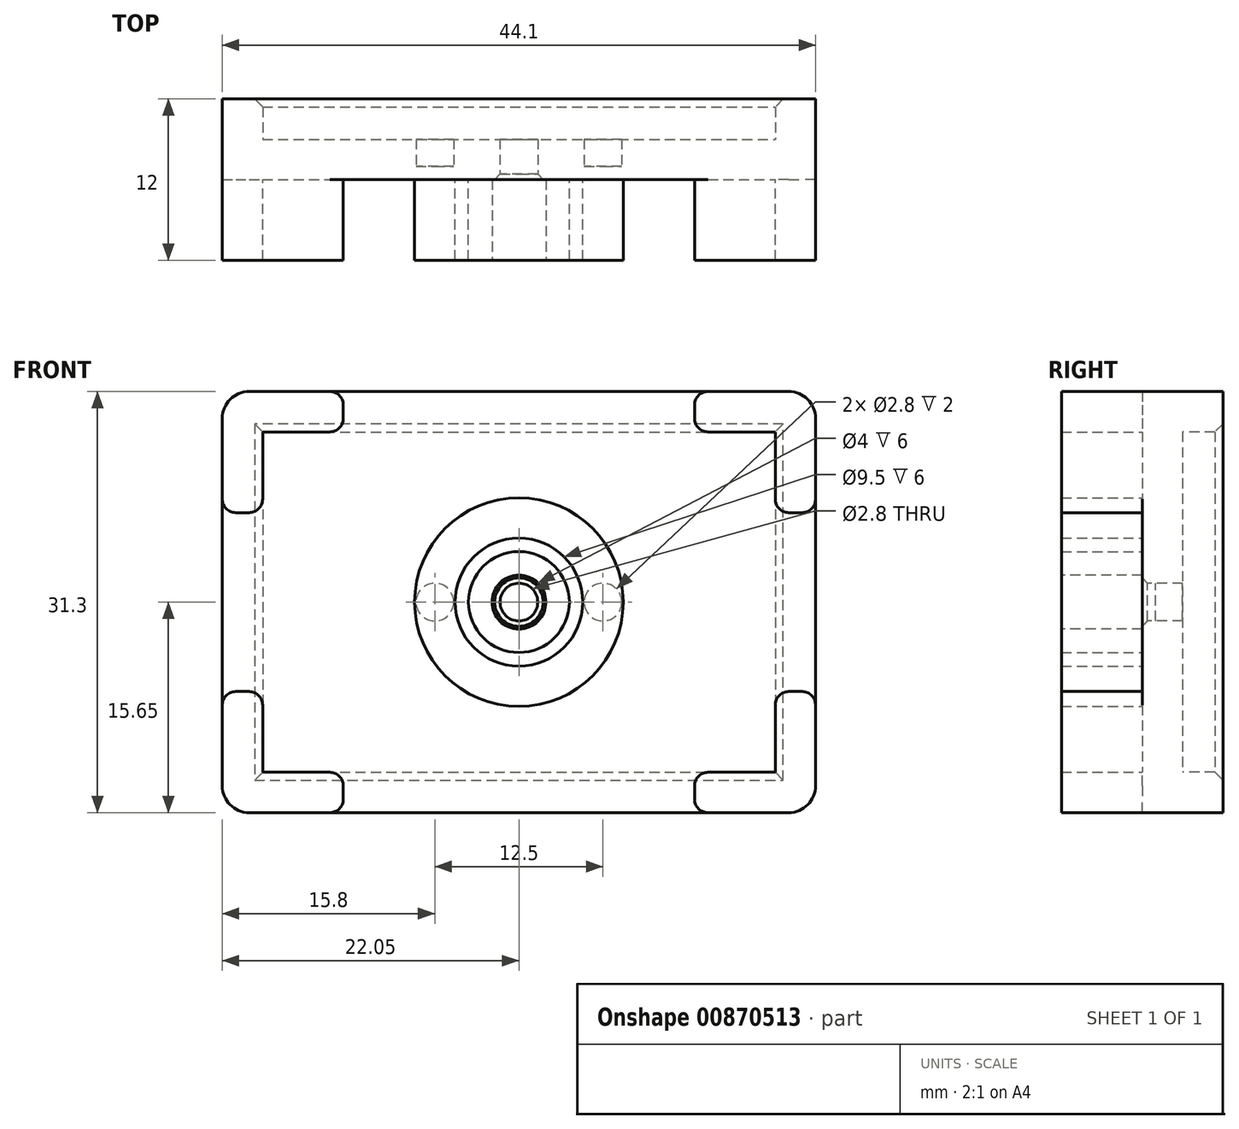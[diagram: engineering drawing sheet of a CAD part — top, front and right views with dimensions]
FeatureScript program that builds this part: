
annotation { "Feature Type Name" : "Feature", "Feature Type Description" : "" }
export const myFeature = defineFeature(function(context is Context, id is Id, definition is map)
    precondition{}
    {
        {
            var Q0;
            Q0=qCreatedBy(makeId("Front.planeOp"),FACE);
            var sketch = newSketch(context, id + "F0", { "sketchPlane" : qUnion([Q0])});
            skLineSegment(sketch, "E0.bottom", {"start": v(-19.05, 12.65) * mm, "end": v(19.05, 12.65) * mm});
            skLineSegment(sketch, "E0.top", {"start": v(-19.05, -12.65) * mm, "end": v(19.05, -12.65) * mm});
            skLineSegment(sketch, "E0.left", {"start": v(-19.05, 12.65) * mm, "end": v(-19.05, -12.65) * mm});
            skLineSegment(sketch, "E0.right", {"start": v(19.05, 12.65) * mm, "end": v(19.05, -12.65) * mm});
            skPoint(sketch, "E0.middle", {"position": v(0, 0) * mm});
            skLineSegment(sketch, "E1.bottom", {"start": v(-22.05, 15.65) * mm, "end": v(22.05, 15.65) * mm});
            skLineSegment(sketch, "E1.top", {"start": v(-22.05, -15.65) * mm, "end": v(22.05, -15.65) * mm});
            skLineSegment(sketch, "E1.left", {"start": v(-22.05, 15.65) * mm, "end": v(-22.05, -15.65) * mm});
            skLineSegment(sketch, "E1.right", {"start": v(22.05, 15.65) * mm, "end": v(22.05, -15.65) * mm});
            skCircle(sketch, "E2", {"center": v(-6.25, 0) * mm, "radius": 1.4 * mm});
            skCircle(sketch, "E3", {"center": v(6.25, 0) * mm, "radius": 1.4 * mm});
            skCircle(sketch, "E4", {"center": v(0, 0) * mm, "radius": 2 * mm});
            skCircle(sketch, "E5", {"center": v(0, 0) * mm, "radius": 4.75 * mm});
            skCircle(sketch, "E6", {"center": v(0, 0) * mm, "radius": 3.75 * mm});
            skCircle(sketch, "E7", {"center": v(0, 0) * mm, "radius": 9.5 * mm});
            skCircle(sketch, "E8", {"center": v(0, 0) * mm, "radius": 7.75 * mm});
            skCircle(sketch, "E9", {"center": v(0, 0) * mm, "radius": 1.4 * mm});
            skLineSegment(sketch, "E10.bottom", {"start": v(-13.05, -12.65) * mm, "end": v(13.05, -12.65) * mm});
            skLineSegment(sketch, "E10.top", {"start": v(-13.05, -15.65) * mm, "end": v(13.05, -15.65) * mm});
            skLineSegment(sketch, "E10.left", {"start": v(-13.05, -12.65) * mm, "end": v(-13.05, -15.65) * mm});
            skLineSegment(sketch, "E10.right", {"start": v(13.05, -12.65) * mm, "end": v(13.05, -15.65) * mm});
            skLineSegment(sketch, "E11.bottom", {"start": v(-13.05, 15.65) * mm, "end": v(13.05, 15.65) * mm});
            skLineSegment(sketch, "E11.top", {"start": v(-13.05, 12.65) * mm, "end": v(13.05, 12.65) * mm});
            skLineSegment(sketch, "E11.left", {"start": v(-13.05, 15.65) * mm, "end": v(-13.05, 12.65) * mm});
            skLineSegment(sketch, "E11.right", {"start": v(13.05, 15.65) * mm, "end": v(13.05, 12.65) * mm});
            skLineSegment(sketch, "E12.bottom", {"start": v(-22.05, -6.65) * mm, "end": v(-19.05, -6.65) * mm});
            skLineSegment(sketch, "E12.top", {"start": v(-22.05, 6.65) * mm, "end": v(-19.05, 6.65) * mm});
            skLineSegment(sketch, "E12.left", {"start": v(-22.05, -6.65) * mm, "end": v(-22.05, 6.65) * mm});
            skLineSegment(sketch, "E12.right", {"start": v(-19.05, -6.65) * mm, "end": v(-19.05, 6.65) * mm});
            skLineSegment(sketch, "E13.bottom", {"start": v(19.05, 6.65) * mm, "end": v(22.05, 6.65) * mm});
            skLineSegment(sketch, "E13.top", {"start": v(19.05, -6.65) * mm, "end": v(22.05, -6.65) * mm});
            skLineSegment(sketch, "E13.left", {"start": v(19.05, 6.65) * mm, "end": v(19.05, -6.65) * mm});
            skLineSegment(sketch, "E13.right", {"start": v(22.05, 6.65) * mm, "end": v(22.05, -6.65) * mm});
            skSolve(sketch);
        }
        {
            var Q0;
            Q0=makeQuery(id+"F0.imprint","IMPRINT",FACE,{"disambiguationData":[TD([[makeQuery(id+"F0.imprint","IMPRINT",EDGE,{"derivedFrom":sQuery(id+"F0.wireOp",EDGE,"E7")}),-1.0]])]});
            var Q1;
            Q1=makeQuery(id+"F0.imprint","IMPRINT",FACE,{"disambiguationData":[TD([[makeQuery(id+"F0.imprint","IMPRINT",EDGE,{"derivedFrom":sQuery(id+"F0.wireOp",EDGE,"E4")}),-1.0]])]});
            var Q2;
            Q2=makeQuery(id+"F0.imprint","IMPRINT",FACE,{"disambiguationData":[TD([[makeQuery(id+"F0.imprint","IMPRINT",EDGE,{"derivedFrom":sQuery(id+"F0.wireOp",EDGE,"E5")}),1.0]])]});
            var Q3;
            Q3=makeQuery(id+"F0.imprint","IMPRINT",FACE,{"disambiguationData":[TD([[makeQuery(id+"F0.imprint","IMPRINT",EDGE,{"derivedFrom":sQuery(id+"F0.wireOp",EDGE,"E2")}),-1.0]])]});
            var Q4;
            Q4=makeQuery(id+"F0.imprint","IMPRINT",FACE,{"disambiguationData":[TD([[makeQuery(id+"F0.imprint","IMPRINT",EDGE,{"derivedFrom":sQuery(id+"F0.wireOp",EDGE,"E7")}),1.0]])]});
            extrude(context, id + "F1", {"entities" : qUnion([Q0, Q1, Q2, Q3, Q4]), "oppositeDirection" : true, "depth" : 3 * mm, "offsetDistance" : 25 * mm});
        }
        {
            var Q0;
            {var subQ7=sQuery(id+"F0.wireOp",EDGE,"E11.right");var subQ13=sQuery(id+"F0.wireOp",EDGE,"E11.left");Q0=qUnion([makeQuery(id+"F0.imprint","IMPRINT",FACE,{"disambiguationData":[TD([[makeQuery(id+"F0.imprint","IMPRINT",EDGE,{"derivedFrom":subQ13}),-1.0]])]}),makeQuery(id+"F0.imprint","IMPRINT",FACE,{"disambiguationData":[TD([[makeQuery(id+"F0.imprint","IMPRINT",EDGE,{"derivedFrom":subQ7}),1.0]])]})]);}
            var Q1;
            {var subQ0=sQuery(id+"F0.wireOp",EDGE,"E10.left");Q1=makeQuery(id+"F0.imprint","IMPRINT",FACE,{"disambiguationData":[TD([[makeQuery(id+"F0.imprint","IMPRINT",EDGE,{"derivedFrom":subQ0}),1.0]])]});}
            var Q2;
            {var subQ0=sQuery(id+"F0.wireOp",EDGE,"E11.left");Q2=makeQuery(id+"F0.imprint","IMPRINT",FACE,{"disambiguationData":[TD([[makeQuery(id+"F0.imprint","IMPRINT",EDGE,{"derivedFrom":subQ0}),1.0]])]});}
            var Q3;
            {var subQ2=sQuery(id+"F0.wireOp",EDGE,"E12.bottom");Q3=makeQuery(id+"F0.imprint","IMPRINT",FACE,{"disambiguationData":[TD([[makeQuery(id+"F0.imprint","IMPRINT",EDGE,{"derivedFrom":subQ2}),1.0]])]});}
            var Q4;
            {var subQ4=sQuery(id+"F0.wireOp",EDGE,"E10.left");Q4=makeQuery(id+"F0.imprint","IMPRINT",FACE,{"disambiguationData":[TD([[makeQuery(id+"F0.imprint","IMPRINT",EDGE,{"derivedFrom":subQ4}),-1.0]])]});}
            var Q5;
            {var subQ4=sQuery(id+"F0.wireOp",EDGE,"E10.right");Q5=makeQuery(id+"F0.imprint","IMPRINT",FACE,{"disambiguationData":[TD([[makeQuery(id+"F0.imprint","IMPRINT",EDGE,{"derivedFrom":subQ4}),1.0]])]});}
            var Q6;
            {var subQ0=sQuery(id+"F0.wireOp",EDGE,"E13.bottom");Q6=makeQuery(id+"F0.imprint","IMPRINT",FACE,{"disambiguationData":[TD([[makeQuery(id+"F0.imprint","IMPRINT",EDGE,{"derivedFrom":subQ0}),-1.0]])]});}
            extrude(context, id + "F2", {"entities" : qUnion([Q0, Q1, Q2, Q3, Q4, Q5, Q6]), "operationType" : NewBodyOperationType.ADD, "oppositeDirection" : true, "depth" : 6 * mm, "offsetDistance" : 25 * mm});
        }
        {
            var Q0;
            Q0=makeQuery(id+"F0.imprint","IMPRINT",FACE,{"disambiguationData":[TD([[makeQuery(id+"F0.imprint","IMPRINT",EDGE,{"derivedFrom":sQuery(id+"F0.wireOp",EDGE,"E2")}),1.0]])]});
            var Q1;
            Q1=makeQuery(id+"F0.imprint","IMPRINT",FACE,{"disambiguationData":[TD([[makeQuery(id+"F0.imprint","IMPRINT",EDGE,{"derivedFrom":sQuery(id+"F0.wireOp",EDGE,"E3")}),1.0]])]});
            extrude(context, id + "F3", {"entities" : qUnion([Q0, Q1]), "operationType" : NewBodyOperationType.ADD, "oppositeDirection" : true, "depth" : 1 * mm, "offsetDistance" : 25 * mm});
        }
        {
            var Q0;
            Q0=makeQuery(id+"F0.imprint","IMPRINT",FACE,{"disambiguationData":[TD([[makeQuery(id+"F0.imprint","IMPRINT",EDGE,{"derivedFrom":sQuery(id+"F0.wireOp",EDGE,"E4")}),-1.0]])]});
            extrude(context, id + "F4", {"entities" : qUnion([Q0]), "operationType" : NewBodyOperationType.ADD, "depth" : 6 * mm, "offsetDistance" : 25 * mm});
        }
        {
            var Q0;
            {var subQ7=sQuery(id+"F0.wireOp",EDGE,"E11.right");var subQ13=sQuery(id+"F0.wireOp",EDGE,"E11.left");Q0=qUnion([makeQuery(id+"F0.imprint","IMPRINT",FACE,{"disambiguationData":[TD([[makeQuery(id+"F0.imprint","IMPRINT",EDGE,{"derivedFrom":subQ13}),-1.0]])]}),makeQuery(id+"F0.imprint","IMPRINT",FACE,{"disambiguationData":[TD([[makeQuery(id+"F0.imprint","IMPRINT",EDGE,{"derivedFrom":subQ7}),1.0]])]})]);}
            var Q1;
            {var subQ4=sQuery(id+"F0.wireOp",EDGE,"E10.left");Q1=makeQuery(id+"F0.imprint","IMPRINT",FACE,{"disambiguationData":[TD([[makeQuery(id+"F0.imprint","IMPRINT",EDGE,{"derivedFrom":subQ4}),-1.0]])]});}
            var Q2;
            {var subQ4=sQuery(id+"F0.wireOp",EDGE,"E10.right");Q2=makeQuery(id+"F0.imprint","IMPRINT",FACE,{"disambiguationData":[TD([[makeQuery(id+"F0.imprint","IMPRINT",EDGE,{"derivedFrom":subQ4}),1.0]])]});}
            extrude(context, id + "F5", {"entities" : qUnion([Q0, Q1, Q2]), "operationType" : NewBodyOperationType.ADD, "depth" : 6 * mm, "offsetDistance" : 25 * mm});
        }
        {
            var Q0;
            Q0=makeQuery(id+"F0.imprint","IMPRINT",FACE,{"disambiguationData":[TD([[makeQuery(id+"F0.imprint","IMPRINT",EDGE,{"derivedFrom":sQuery(id+"F0.wireOp",EDGE,"E2")}),-1.0]])]});
            var Q1;
            Q1=makeQuery(id+"F0.imprint","IMPRINT",FACE,{"disambiguationData":[TD([[makeQuery(id+"F0.imprint","IMPRINT",EDGE,{"derivedFrom":sQuery(id+"F0.wireOp",EDGE,"E2")}),1.0]])]});
            var Q2;
            Q2=makeQuery(id+"F0.imprint","IMPRINT",FACE,{"disambiguationData":[TD([[makeQuery(id+"F0.imprint","IMPRINT",EDGE,{"derivedFrom":sQuery(id+"F0.wireOp",EDGE,"E3")}),1.0]])]});
            extrude(context, id + "F6", {"entities" : qUnion([Q0, Q1, Q2]), "operationType" : NewBodyOperationType.ADD, "depth" : 6 * mm, "offsetDistance" : 25 * mm});
        }
        {
            var Q0;
            Q0=makeQuery(id+"F2.opExtrude","CAP_EDGE",EDGE,{"disambiguationData":[OSD([sQuery(id+"F0.wireOp",EDGE,"E0.bottom")])],"isStart":false});
            var Q1;
            Q1=makeQuery(id+"F2.opExtrude","CAP_EDGE",EDGE,{"disambiguationData":[OSD([sQuery(id+"F0.wireOp",EDGE,"E0.left")])],"isStart":false});
            var Q2;
            Q2=makeQuery(id+"F2.opExtrude","CAP_EDGE",EDGE,{"disambiguationData":[OSD([sQuery(id+"F0.wireOp",EDGE,"E0.right")])],"isStart":false});
            var Q3;
            Q3=makeQuery(id+"F2.opExtrude","CAP_EDGE",EDGE,{"disambiguationData":[OSD([sQuery(id+"F0.wireOp",EDGE,"E0.top")])],"isStart":false});
            chamfer(context, id + "F7", {"entities" : qUnion([Q0, Q1, Q2, Q3]), "width" : 0.6 * mm, "tangentPropagation" : true});
        }
        {
            var Q0;
            Q0=makeQuery(id+"F0.imprint","IMPRINT",FACE,{"disambiguationData":[TD([[makeQuery(id+"F0.imprint","IMPRINT",EDGE,{"derivedFrom":sQuery(id+"F0.wireOp",EDGE,"E4")}),1.0]])]});
            extrude(context, id + "F8", {"entities" : qUnion([Q0]), "operationType" : NewBodyOperationType.ADD, "oppositeDirection" : true, "depth" : 3 * mm, "offsetDistance" : 25 * mm});
        }
        {
            var Q0;
            {var subQ0=sQuery(id+"F0.wireOp",EDGE,"E1.right");var subQ1=sQuery(id+"F0.wireOp",EDGE,"E1.bottom");Q0=makeQuery(id+"F5.boolean.opBoolean","MERGE",EDGE,{"derivedFrom":[makeQuery(id+"F2.opExtrude","SWEPT_EDGE",EDGE,{"disambiguationData":[OSD([subQ1,subQ0])]}),makeQuery(id+"F5.opExtrude","SWEPT_EDGE",EDGE,{"disambiguationData":[OSD([subQ1,subQ0])]})]});}
            var Q1;
            {var subQ0=sQuery(id+"F0.wireOp",EDGE,"E1.left");var subQ1=sQuery(id+"F0.wireOp",EDGE,"E1.bottom");Q1=makeQuery(id+"F5.boolean.opBoolean","MERGE",EDGE,{"derivedFrom":[makeQuery(id+"F2.opExtrude","SWEPT_EDGE",EDGE,{"disambiguationData":[OSD([subQ1,subQ0])]}),makeQuery(id+"F5.opExtrude","SWEPT_EDGE",EDGE,{"disambiguationData":[OSD([subQ1,subQ0])]})]});}
            var Q2;
            {var subQ0=sQuery(id+"F0.wireOp",EDGE,"E1.left");var subQ1=sQuery(id+"F0.wireOp",EDGE,"E1.top");Q2=makeQuery(id+"F5.boolean.opBoolean","MERGE",EDGE,{"derivedFrom":[makeQuery(id+"F2.opExtrude","SWEPT_EDGE",EDGE,{"disambiguationData":[OSD([subQ1,subQ0])]}),makeQuery(id+"F5.opExtrude","SWEPT_EDGE",EDGE,{"disambiguationData":[OSD([subQ1,subQ0])]})]});}
            var Q3;
            {var subQ0=sQuery(id+"F0.wireOp",EDGE,"E1.right");var subQ1=sQuery(id+"F0.wireOp",EDGE,"E1.top");Q3=makeQuery(id+"F5.boolean.opBoolean","MERGE",EDGE,{"derivedFrom":[makeQuery(id+"F2.opExtrude","SWEPT_EDGE",EDGE,{"disambiguationData":[OSD([subQ1,subQ0])]}),makeQuery(id+"F5.opExtrude","SWEPT_EDGE",EDGE,{"disambiguationData":[OSD([subQ1,subQ0])]})]});}
            fillet(context, id + "F9", {"entities" : qUnion([Q0, Q1, Q2, Q3]), "radius" : 2 * mm, "tangentPropagation" : true, "allowEdgeOverflow" : false});
        }
        {
            var Q0;
            Q0=makeQuery(id+"F8.opExtrude","CAP_EDGE",EDGE,{"disambiguationData":[OSD([sQuery(id+"F0.wireOp",EDGE,"E9")])],"isStart":true});
            chamfer(context, id + "F10", {"entities" : qUnion([Q0]), "width" : 0.4 * mm, "tangentPropagation" : true});
        }
        {
            var Q0;
            Q0=makeQuery(id+"F5.opExtrude","SWEPT_EDGE",EDGE,{"disambiguationData":[OSD([sQuery(id+"F0.wireOp",EDGE,"E1.left"),sQuery(id+"F0.wireOp",EDGE,"E12.top")])]});
            var Q1;
            Q1=makeQuery(id+"F5.opExtrude","SWEPT_EDGE",EDGE,{"disambiguationData":[OSD([sQuery(id+"F0.wireOp",EDGE,"E0.left"),sQuery(id+"F0.wireOp",EDGE,"E12.top")])]});
            var Q2;
            Q2=makeQuery(id+"F5.opExtrude","SWEPT_EDGE",EDGE,{"disambiguationData":[OSD([sQuery(id+"F0.wireOp",EDGE,"E0.bottom"),sQuery(id+"F0.wireOp",EDGE,"E11.left")])]});
            var Q3;
            Q3=makeQuery(id+"F5.opExtrude","SWEPT_EDGE",EDGE,{"disambiguationData":[OSD([sQuery(id+"F0.wireOp",EDGE,"E1.bottom"),sQuery(id+"F0.wireOp",EDGE,"E11.left")])]});
            var Q4;
            Q4=makeQuery(id+"F5.opExtrude","SWEPT_EDGE",EDGE,{"disambiguationData":[OSD([sQuery(id+"F0.wireOp",EDGE,"E0.bottom"),sQuery(id+"F0.wireOp",EDGE,"E11.right")])]});
            var Q5;
            Q5=makeQuery(id+"F5.opExtrude","SWEPT_EDGE",EDGE,{"disambiguationData":[OSD([sQuery(id+"F0.wireOp",EDGE,"E0.right"),sQuery(id+"F0.wireOp",EDGE,"E13.bottom")])]});
            var Q6;
            Q6=makeQuery(id+"F5.opExtrude","SWEPT_EDGE",EDGE,{"disambiguationData":[OSD([sQuery(id+"F0.wireOp",EDGE,"E1.right"),sQuery(id+"F0.wireOp",EDGE,"E13.bottom")])]});
            var Q7;
            Q7=makeQuery(id+"F5.opExtrude","SWEPT_EDGE",EDGE,{"disambiguationData":[OSD([sQuery(id+"F0.wireOp",EDGE,"E1.top"),sQuery(id+"F0.wireOp",EDGE,"E10.left")])]});
            var Q8;
            Q8=makeQuery(id+"F5.opExtrude","SWEPT_EDGE",EDGE,{"disambiguationData":[OSD([sQuery(id+"F0.wireOp",EDGE,"E1.top"),sQuery(id+"F0.wireOp",EDGE,"E10.right")])]});
            var Q9;
            Q9=makeQuery(id+"F5.opExtrude","SWEPT_EDGE",EDGE,{"disambiguationData":[OSD([sQuery(id+"F0.wireOp",EDGE,"E1.left"),sQuery(id+"F0.wireOp",EDGE,"E12.bottom")])]});
            var Q10;
            Q10=makeQuery(id+"F5.opExtrude","SWEPT_EDGE",EDGE,{"disambiguationData":[OSD([sQuery(id+"F0.wireOp",EDGE,"E0.left"),sQuery(id+"F0.wireOp",EDGE,"E12.bottom")])]});
            var Q11;
            Q11=makeQuery(id+"F5.opExtrude","SWEPT_EDGE",EDGE,{"disambiguationData":[OSD([sQuery(id+"F0.wireOp",EDGE,"E1.bottom"),sQuery(id+"F0.wireOp",EDGE,"E11.right")])]});
            var Q12;
            Q12=makeQuery(id+"F5.opExtrude","SWEPT_EDGE",EDGE,{"disambiguationData":[OSD([sQuery(id+"F0.wireOp",EDGE,"E1.right"),sQuery(id+"F0.wireOp",EDGE,"E13.top")])]});
            var Q13;
            Q13=makeQuery(id+"F5.opExtrude","SWEPT_EDGE",EDGE,{"disambiguationData":[OSD([sQuery(id+"F0.wireOp",EDGE,"E0.right"),sQuery(id+"F0.wireOp",EDGE,"E13.top")])]});
            var Q14;
            Q14=makeQuery(id+"F5.opExtrude","SWEPT_EDGE",EDGE,{"disambiguationData":[OSD([sQuery(id+"F0.wireOp",EDGE,"E0.top"),sQuery(id+"F0.wireOp",EDGE,"E10.right")])]});
            var Q15;
            Q15=makeQuery(id+"F5.opExtrude","SWEPT_EDGE",EDGE,{"disambiguationData":[OSD([sQuery(id+"F0.wireOp",EDGE,"E0.top"),sQuery(id+"F0.wireOp",EDGE,"E10.left")])]});
            fillet(context, id + "F11", {"entities" : qUnion([Q0, Q1, Q2, Q3, Q4, Q5, Q6, Q7, Q8, Q9, Q10, Q11, Q12, Q13, Q14, Q15]), "radius" : 1 * mm, "tangentPropagation" : true, "allowEdgeOverflow" : false});
        }
    });
